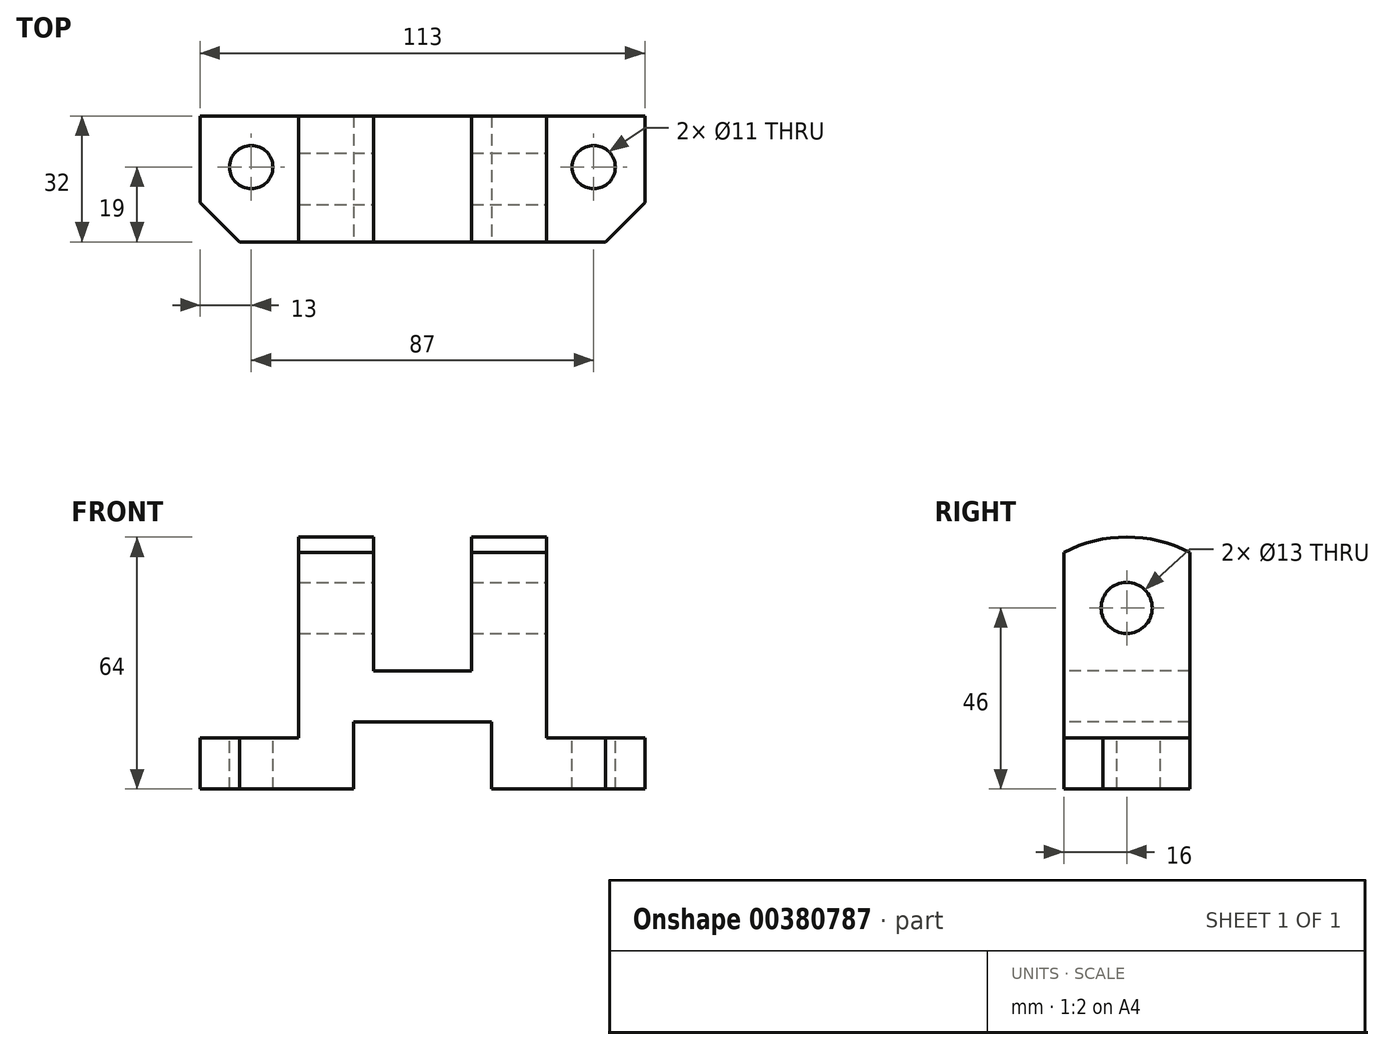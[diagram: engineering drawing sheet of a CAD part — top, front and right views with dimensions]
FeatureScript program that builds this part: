
annotation { "Feature Type Name" : "Feature", "Feature Type Description" : "" }
export const myFeature = defineFeature(function(context is Context, id is Id, definition is map)
    precondition{}
    {
        {
            var Q0;
            Q0=qCreatedBy(makeId("Top.planeOp"),FACE);
            var sketch = newSketch(context, id + "F0", { "sketchPlane" : qUnion([Q0])});
            skLineSegment(sketch, "E0.bottom", {"start": v(0, 0) * mm, "end": v(113, 0) * mm});
            skLineSegment(sketch, "E0.top", {"start": v(0, 32) * mm, "end": v(113, 32) * mm});
            skLineSegment(sketch, "E0.left", {"start": v(0, 0) * mm, "end": v(0, 32) * mm});
            skLineSegment(sketch, "E0.right", {"start": v(113, 0) * mm, "end": v(113, 32) * mm});
            skSolve(sketch);
        }
        {
            var Q0;
            Q0=makeQuery(id+"F0.imprint","IMPRINT",FACE,{"disambiguationData":[TD([[makeQuery(id+"F0.imprint","IMPRINT",EDGE,{"derivedFrom":sQuery(id+"F0.wireOp",EDGE,"E0.bottom")}),1.0]])]});
            extrude(context, id + "F1", {"entities" : qUnion([Q0]), "depth" : 64 * mm});
        }
        {
            var Q0;
            Q0=makeQuery(id+"F1.opExtrude","SWEPT_FACE",FACE,{"disambiguationData":[OSD([sQuery(id+"F0.wireOp",EDGE,"E0.bottom")])]});
            var sketch = newSketch(context, id + "F2", { "sketchPlane" : qUnion([Q0])});
            skLineSegment(sketch, "E1.bottom", {"start": v(39, 0) * mm, "end": v(74, 0) * mm});
            skLineSegment(sketch, "E1.top", {"start": v(39, 17) * mm, "end": v(74, 17) * mm});
            skLineSegment(sketch, "E1.left", {"start": v(39, 0) * mm, "end": v(39, 17) * mm});
            skLineSegment(sketch, "E1.right", {"start": v(74, 0) * mm, "end": v(74, 17) * mm});
            skSolve(sketch);
        }
        {
            var Q0;
            Q0=makeQuery(id+"F2.imprint","IMPRINT",FACE,{"disambiguationData":[TD([[makeQuery(id+"F2.imprint","IMPRINT",EDGE,{"derivedFrom":sQuery(id+"F2.wireOp",EDGE,"E1.bottom")}),1.0]])]});
            extrude(context, id + "F3", {"entities" : qUnion([Q0]), "operationType" : NewBodyOperationType.REMOVE, "endBound" : BoundingType.THROUGH_ALL, "oppositeDirection" : true, "depth" : 25 * mm});
        }
        {
            var Q0;
            Q0=makeQuery(id+"F1.opExtrude","SWEPT_FACE",FACE,{"disambiguationData":[OSD([sQuery(id+"F0.wireOp",EDGE,"E0.bottom")])]});
            var sketch = newSketch(context, id + "F4", { "sketchPlane" : qUnion([Q0])});
            skLineSegment(sketch, "E2.bottom", {"start": v(44, 64) * mm, "end": v(69, 64) * mm});
            skLineSegment(sketch, "E2.top", {"start": v(44, 30) * mm, "end": v(69, 30) * mm});
            skLineSegment(sketch, "E2.left", {"start": v(44, 64) * mm, "end": v(44, 30) * mm});
            skLineSegment(sketch, "E2.right", {"start": v(69, 64) * mm, "end": v(69, 30) * mm});
            skSolve(sketch);
        }
        {
            var Q0;
            Q0=makeQuery(id+"F4.imprint","IMPRINT",FACE,{"disambiguationData":[TD([[makeQuery(id+"F4.imprint","IMPRINT",EDGE,{"derivedFrom":sQuery(id+"F4.wireOp",EDGE,"E2.bottom")}),-1.0]])]});
            extrude(context, id + "F5", {"entities" : qUnion([Q0]), "operationType" : NewBodyOperationType.REMOVE, "endBound" : BoundingType.THROUGH_ALL, "oppositeDirection" : true, "depth" : 25 * mm});
        }
        {
            var Q0;
            Q0=makeQuery(id+"F1.opExtrude","SWEPT_FACE",FACE,{"disambiguationData":[OSD([sQuery(id+"F0.wireOp",EDGE,"E0.bottom")])]});
            var sketch = newSketch(context, id + "F6", { "sketchPlane" : qUnion([Q0])});
            skLineSegment(sketch, "E3.bottom", {"start": v(113, 64) * mm, "end": v(88, 64) * mm});
            skLineSegment(sketch, "E3.top", {"start": v(113, 13) * mm, "end": v(88, 13) * mm});
            skLineSegment(sketch, "E3.left", {"start": v(113, 64) * mm, "end": v(113, 13) * mm});
            skLineSegment(sketch, "E3.right", {"start": v(88, 64) * mm, "end": v(88, 13) * mm});
            skLineSegment(sketch, "E4.bottom", {"start": v(0, 64) * mm, "end": v(25, 64) * mm});
            skLineSegment(sketch, "E4.top", {"start": v(0, 13) * mm, "end": v(25, 13) * mm});
            skLineSegment(sketch, "E4.left", {"start": v(0, 64) * mm, "end": v(0, 13) * mm});
            skLineSegment(sketch, "E4.right", {"start": v(25, 64) * mm, "end": v(25, 13) * mm});
            skSolve(sketch);
        }
        {
            var Q0;
            Q0=makeQuery(id+"F6.imprint","IMPRINT",FACE,{"disambiguationData":[TD([[makeQuery(id+"F6.imprint","IMPRINT",EDGE,{"derivedFrom":sQuery(id+"F6.wireOp",EDGE,"E3.bottom")}),-1.0]])]});
            var Q1;
            Q1=makeQuery(id+"F6.imprint","IMPRINT",FACE,{"disambiguationData":[TD([[makeQuery(id+"F6.imprint","IMPRINT",EDGE,{"derivedFrom":sQuery(id+"F6.wireOp",EDGE,"E4.bottom")}),-1.0]])]});
            extrude(context, id + "F7", {"entities" : qUnion([Q0, Q1]), "operationType" : NewBodyOperationType.REMOVE, "endBound" : BoundingType.THROUGH_ALL, "oppositeDirection" : true, "depth" : 25 * mm});
        }
        {
            var Q0;
            Q0=makeQuery(id+"F7.boolean.opBoolean","COPY",FACE,{"derivedFrom":makeQuery(id+"F7.opExtrude","SWEPT_FACE",FACE,{"disambiguationData":[OSD([sQuery(id+"F6.wireOp",EDGE,"E3.top")])]})});
            var sketch = newSketch(context, id + "F8", { "sketchPlane" : qUnion([Q0])});
            skCircle(sketch, "E5", {"center": v(100, 19) * mm, "radius": 5.5 * mm});
            skSolve(sketch);
        }
        {
            var Q0;
            Q0=makeQuery(id+"F7.boolean.opBoolean","COPY",FACE,{"derivedFrom":makeQuery(id+"F7.opExtrude","SWEPT_FACE",FACE,{"disambiguationData":[OSD([sQuery(id+"F6.wireOp",EDGE,"E4.top")])]})});
            var sketch = newSketch(context, id + "F9", { "sketchPlane" : qUnion([Q0])});
            skCircle(sketch, "E6", {"center": v(13, 19) * mm, "radius": 5.5 * mm});
            skSolve(sketch);
        }
        {
            var Q0;
            Q0=makeQuery(id+"F9.imprint","IMPRINT",FACE,{"disambiguationData":[TD([[makeQuery(id+"F9.imprint","IMPRINT",EDGE,{"derivedFrom":sQuery(id+"F9.wireOp",EDGE,"E6")}),1.0]])]});
            var Q1;
            Q1=makeQuery(id+"F8.imprint","IMPRINT",FACE,{"disambiguationData":[TD([[makeQuery(id+"F8.imprint","IMPRINT",EDGE,{"derivedFrom":sQuery(id+"F8.wireOp",EDGE,"E5")}),1.0]])]});
            extrude(context, id + "F10", {"entities" : qUnion([Q0, Q1]), "operationType" : NewBodyOperationType.REMOVE, "endBound" : BoundingType.THROUGH_ALL, "oppositeDirection" : true, "depth" : 25 * mm});
        }
        {
            var Q0;
            Q0=makeQuery(id+"F7.boolean.opBoolean","COPY",FACE,{"derivedFrom":makeQuery(id+"F7.opExtrude","SWEPT_FACE",FACE,{"disambiguationData":[OSD([sQuery(id+"F6.wireOp",EDGE,"E3.right")])]})});
            var sketch = newSketch(context, id + "F11", { "sketchPlane" : qUnion([Q0])});
            skCircle(sketch, "E7", {"center": v(16, 46) * mm, "radius": 6.5 * mm});
            skSolve(sketch);
        }
        {
            var Q0;
            Q0=makeQuery(id+"F11.imprint","IMPRINT",FACE,{"disambiguationData":[TD([[makeQuery(id+"F11.imprint","IMPRINT",EDGE,{"derivedFrom":sQuery(id+"F11.wireOp",EDGE,"E7")}),1.0]])]});
            extrude(context, id + "F12", {"entities" : qUnion([Q0]), "operationType" : NewBodyOperationType.REMOVE, "endBound" : BoundingType.THROUGH_ALL, "oppositeDirection" : true, "depth" : 25 * mm});
        }
        {
            var Q0;
            Q0=makeQuery(id+"F7.boolean.opBoolean","COPY",FACE,{"derivedFrom":makeQuery(id+"F7.opExtrude","SWEPT_FACE",FACE,{"disambiguationData":[OSD([sQuery(id+"F6.wireOp",EDGE,"E3.top")])]})});
            var sketch = newSketch(context, id + "F13", { "sketchPlane" : qUnion([Q0])});
            skLineSegment(sketch, "E8", {"start": v(113, 10) * mm, "end": v(103, 0) * mm});
            skLineSegment(sketch, "E9", {"start": v(103, 0) * mm, "end": v(113, 0) * mm});
            skLineSegment(sketch, "E10", {"start": v(113, 0) * mm, "end": v(113, 10) * mm});
            skSolve(sketch);
        }
        {
            var Q0;
            Q0=makeQuery(id+"F7.boolean.opBoolean","COPY",FACE,{"derivedFrom":makeQuery(id+"F7.opExtrude","SWEPT_FACE",FACE,{"disambiguationData":[OSD([sQuery(id+"F6.wireOp",EDGE,"E4.top")])]})});
            var sketch = newSketch(context, id + "F14", { "sketchPlane" : qUnion([Q0])});
            skLineSegment(sketch, "E11", {"start": v(0, 10) * mm, "end": v(10, 0) * mm});
            skLineSegment(sketch, "E12", {"start": v(10, 0) * mm, "end": v(0, 0) * mm});
            skLineSegment(sketch, "E13", {"start": v(0, 0) * mm, "end": v(0, 10) * mm});
            skSolve(sketch);
        }
        {
            var Q0;
            Q0=makeQuery(id+"F14.imprint","IMPRINT",FACE,{"disambiguationData":[TD([[makeQuery(id+"F14.imprint","IMPRINT",EDGE,{"derivedFrom":sQuery(id+"F14.wireOp",EDGE,"E11")}),-1.0]])]});
            var Q1;
            Q1=makeQuery(id+"F13.imprint","IMPRINT",FACE,{"disambiguationData":[TD([[makeQuery(id+"F13.imprint","IMPRINT",EDGE,{"derivedFrom":sQuery(id+"F13.wireOp",EDGE,"E8")}),1.0]])]});
            extrude(context, id + "F15", {"entities" : qUnion([Q0, Q1]), "operationType" : NewBodyOperationType.REMOVE, "endBound" : BoundingType.THROUGH_ALL, "oppositeDirection" : true, "depth" : 25 * mm});
        }
        {
            var Q0;
            Q0=makeQuery(id+"F7.boolean.opBoolean","COPY",FACE,{"derivedFrom":makeQuery(id+"F7.opExtrude","SWEPT_FACE",FACE,{"disambiguationData":[OSD([sQuery(id+"F6.wireOp",EDGE,"E3.right")])]})});
            var sketch = newSketch(context, id + "F16", { "sketchPlane" : qUnion([Q0])});
            skArc(sketch, "E14", {"start": v(32, 60.13) * mm, "mid": v(16, 64) * mm, "end": v(0, 60.13) * mm});
            skSolve(sketch);
        }
        {
            var Q0;
            {var subQ0=sQuery(id+"F16.wireOp",EDGE,"E14");var subQ1=sQuery(id+"F6.wireOp",EDGE,"E3.right");var subQ2=makeQuery(id+"F7.boolean.opBoolean","COPY",EDGE,{"derivedFrom":makeQuery(id+"F7.opExtrude","CAP_EDGE",EDGE,{"disambiguationData":[OSD([subQ1])],"isStart":true})});var subQ3=makeQuery(id+"F16.imprint","INTERSECT",VERTEX,{"derivedFrom":[subQ2,subQ0]});Q0=makeQuery(id+"F16.imprint","IMPRINT",FACE,{"disambiguationData":[TD([[makeQuery(id+"F16.imprint","IMPRINT",EDGE,{"disambiguationData":[TD([[subQ3,1.0]])],"derivedFrom":subQ0}),-1.0]])]});}
            var Q1;
            {var subQ0=sQuery(id+"F16.wireOp",EDGE,"E14");var subQ1=sQuery(id+"F6.wireOp",EDGE,"E3.right");var subQ2=makeQuery(id+"F7.boolean.opBoolean","INTERSECT",EDGE,{"derivedFrom":[makeQuery(id+"F1.opExtrude","SWEPT_FACE",FACE,{"disambiguationData":[OSD([sQuery(id+"F0.wireOp",EDGE,"E0.top")])]}),makeQuery(id+"F7.opExtrude","SWEPT_FACE",FACE,{"disambiguationData":[OSD([subQ1])]})]});var subQ3=makeQuery(id+"F16.imprint","INTERSECT",VERTEX,{"derivedFrom":[subQ2,subQ0]});Q1=makeQuery(id+"F16.imprint","IMPRINT",FACE,{"disambiguationData":[TD([[makeQuery(id+"F16.imprint","IMPRINT",EDGE,{"disambiguationData":[TD([[subQ3,-1.0]])],"derivedFrom":subQ0}),-1.0]])]});}
            extrude(context, id + "F17", {"entities" : qUnion([Q0, Q1]), "operationType" : NewBodyOperationType.REMOVE, "endBound" : BoundingType.THROUGH_ALL, "oppositeDirection" : true, "depth" : 25 * mm});
        }
    });
